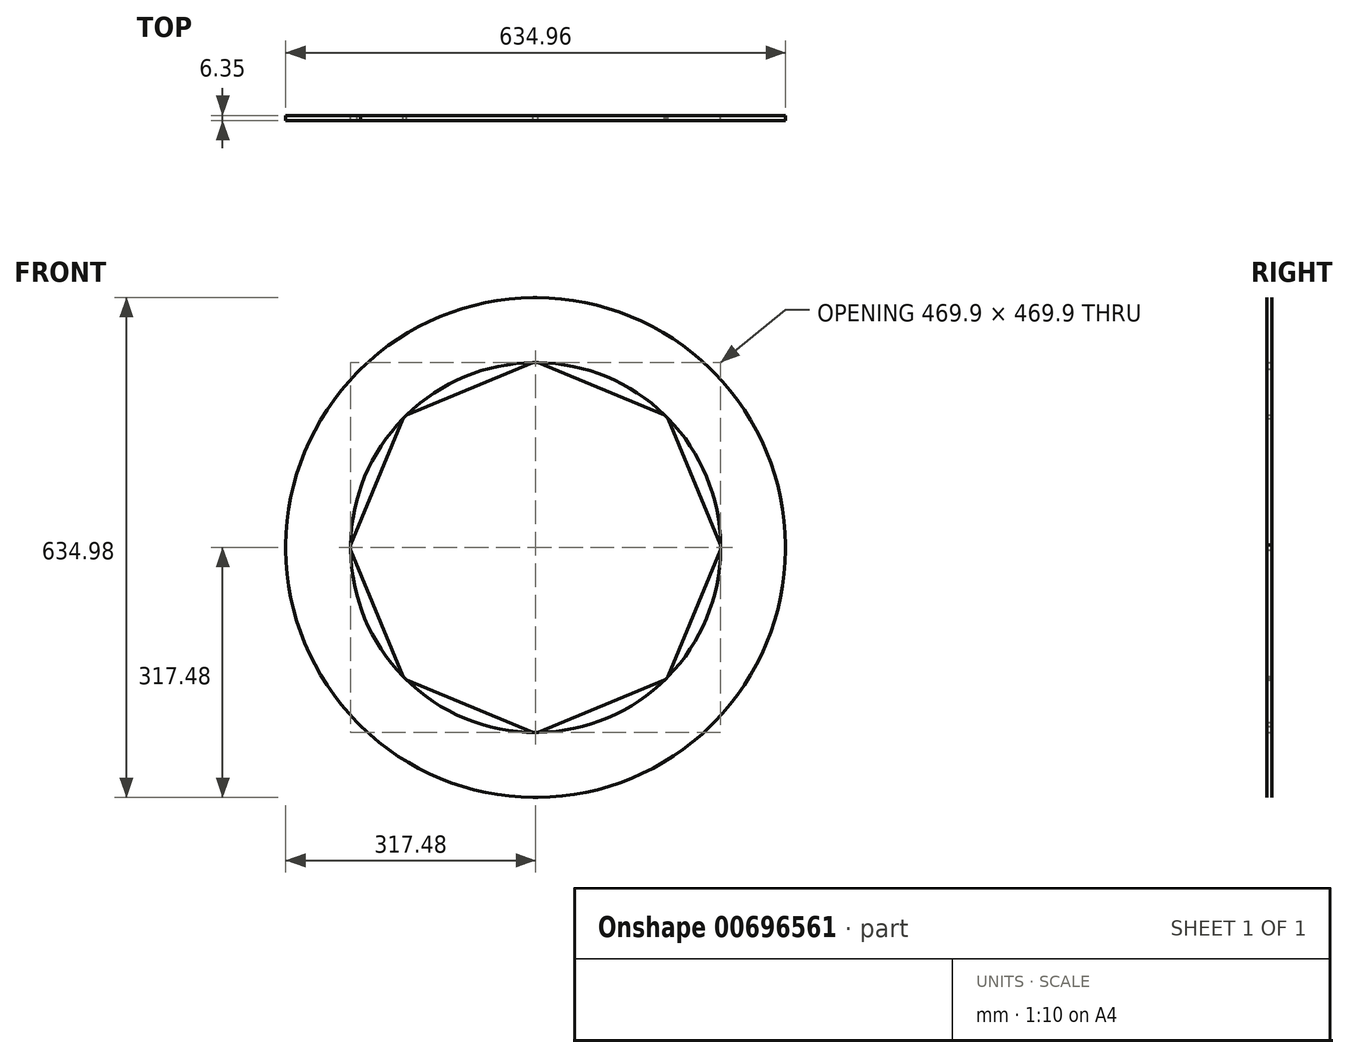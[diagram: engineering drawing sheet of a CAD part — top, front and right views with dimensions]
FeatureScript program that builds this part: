
annotation { "Feature Type Name" : "Feature", "Feature Type Description" : "" }
export const myFeature = defineFeature(function(context is Context, id is Id, definition is map)
    precondition{}
    {
        {
            var Q0;
            Q0=qCreatedBy(makeId("Front.planeOp"),FACE);
            var sketch = newSketch(context, id + "F0", { "sketchPlane" : qUnion([Q0])});
            skCircle(sketch, "E0", {"center": v(0, 0) * mm, "radius": 234.95 * mm});
            skCircle(sketch, "E1", {"center": v(0, 0) * mm, "radius": 317.5 * mm});
            skLineSegment(sketch, "E2", {"start": v(317.48, 0) * mm, "end": v(317.5, 0) * mm});
            skLineSegment(sketch, "E3", {"start": v(317.5, 0) * mm, "end": v(317.48, 0) * mm});
            skLineSegment(sketch, "E4", {"start": v(-317.48, 0) * mm, "end": v(-317.5, 0) * mm});
            skLineSegment(sketch, "E5", {"start": v(0, 317.5) * mm, "end": v(0, 317.5) * mm});
            skLineSegment(sketch, "E6", {"start": v(0, -317.48) * mm, "end": v(0, -317.5) * mm});
            skLineSegment(sketch, "E7.bottom", {"start": v(-317.5, 0) * mm, "end": v(-317.48, 0) * mm});
            skLineSegment(sketch, "E8", {"start": v(-224.5, 224.5) * mm, "end": v(-224.5, 224.5) * mm});
            skLineSegment(sketch, "E9", {"start": v(224.5, 224.5) * mm, "end": v(224.5, 224.5) * mm});
            skLineSegment(sketch, "E10", {"start": v(-224.5, -224.5) * mm, "end": v(-224.5, -224.5) * mm});
            skLineSegment(sketch, "E11", {"start": v(224.5, -224.5) * mm, "end": v(224.5, -224.5) * mm});
            skLineSegment(sketch, "E12", {"start": v(-166.13, -166.13) * mm, "end": v(-163.87, -168.36) * mm});
            skLineSegment(sketch, "E13", {"start": v(-166.13, -166.13) * mm, "end": v(-168.38, -163.89) * mm});
            skLineSegment(sketch, "E14", {"start": v(-168.38, -163.89) * mm, "end": v(-226.74, -222.25) * mm});
            skLineSegment(sketch, "E15", {"start": v(-163.87, -168.36) * mm, "end": v(-221.85, -227.13) * mm});
            skLineSegment(sketch, "E16", {"start": v(-221.85, -227.13) * mm, "end": v(-226.74, -222.25) * mm});
            skLineSegment(sketch, "E17", {"start": v(0, -234.95) * mm, "end": v(-3.17, -234.93) * mm});
            skLineSegment(sketch, "E18", {"start": v(0, -234.95) * mm, "end": v(3.18, -234.95) * mm});
            skLineSegment(sketch, "E19", {"start": v(-3.17, -234.93) * mm, "end": v(-3.17, -317.48) * mm});
            skLineSegment(sketch, "E20", {"start": v(3.18, -234.95) * mm, "end": v(3.18, -317.48) * mm});
            skLineSegment(sketch, "E21", {"start": v(3.18, -317.48) * mm, "end": v(-3.17, -317.48) * mm});
            skLineSegment(sketch, "E22", {"start": v(166.13, -166.13) * mm, "end": v(163.74, -168.22) * mm});
            skLineSegment(sketch, "E23", {"start": v(166.13, -166.13) * mm, "end": v(168.38, -163.89) * mm});
            skLineSegment(sketch, "E24", {"start": v(163.74, -168.22) * mm, "end": v(222.26, -226.73) * mm});
            skLineSegment(sketch, "E25", {"start": v(168.38, -163.89) * mm, "end": v(226.74, -222.25) * mm});
            skLineSegment(sketch, "E26", {"start": v(226.74, -222.25) * mm, "end": v(222.26, -226.73) * mm});
            skLineSegment(sketch, "E27", {"start": v(234.95, 0) * mm, "end": v(234.95, -3.17) * mm});
            skLineSegment(sketch, "E28", {"start": v(234.95, 0) * mm, "end": v(234.95, 3.18) * mm});
            skLineSegment(sketch, "E29", {"start": v(234.95, 3.18) * mm, "end": v(317.48, 3.18) * mm});
            skLineSegment(sketch, "E30", {"start": v(317.48, 3.18) * mm, "end": v(317.48, -3.18) * mm});
            skLineSegment(sketch, "E31", {"start": v(317.48, -3.18) * mm, "end": v(234.95, -3.17) * mm});
            skLineSegment(sketch, "E32", {"start": v(166.13, 166.13) * mm, "end": v(168.38, 163.89) * mm});
            skLineSegment(sketch, "E33", {"start": v(166.13, 166.13) * mm, "end": v(163.89, 168.38) * mm});
            skLineSegment(sketch, "E34", {"start": v(168.38, 163.89) * mm, "end": v(226.74, 222.25) * mm});
            skLineSegment(sketch, "E35", {"start": v(226.74, 222.25) * mm, "end": v(222.25, 226.74) * mm});
            skLineSegment(sketch, "E36", {"start": v(222.25, 226.74) * mm, "end": v(163.89, 168.38) * mm});
            skLineSegment(sketch, "E37", {"start": v(0, 234.95) * mm, "end": v(3.17, 234.95) * mm});
            skLineSegment(sketch, "E38", {"start": v(0, 234.95) * mm, "end": v(-3.17, 234.95) * mm});
            skLineSegment(sketch, "E39", {"start": v(-3.17, 234.95) * mm, "end": v(-3.17, 317.48) * mm});
            skLineSegment(sketch, "E40", {"start": v(-3.17, 317.48) * mm, "end": v(3.17, 317.5) * mm});
            skLineSegment(sketch, "E41", {"start": v(3.17, 317.5) * mm, "end": v(3.17, 234.95) * mm});
            skLineSegment(sketch, "E42", {"start": v(-166.13, 166.13) * mm, "end": v(-168.38, 163.89) * mm});
            skLineSegment(sketch, "E43", {"start": v(-166.13, 166.13) * mm, "end": v(-163.89, 168.38) * mm});
            skLineSegment(sketch, "E44", {"start": v(-168.38, 163.89) * mm, "end": v(-226.74, 222.25) * mm});
            skLineSegment(sketch, "E45", {"start": v(-226.74, 222.25) * mm, "end": v(-222.25, 226.74) * mm});
            skLineSegment(sketch, "E46", {"start": v(-222.25, 226.74) * mm, "end": v(-163.89, 168.38) * mm});
            skLineSegment(sketch, "E47", {"start": v(-234.95, 0) * mm, "end": v(-234.95, -3.18) * mm});
            skLineSegment(sketch, "E48", {"start": v(-234.95, 0) * mm, "end": v(-234.95, 3.17) * mm});
            skLineSegment(sketch, "E49", {"start": v(-234.95, 3.17) * mm, "end": v(-317.48, 3.17) * mm});
            skLineSegment(sketch, "E50", {"start": v(-317.48, 3.17) * mm, "end": v(-317.48, -3.18) * mm});
            skLineSegment(sketch, "E51", {"start": v(-317.48, -3.17) * mm, "end": v(-234.95, -3.18) * mm});
            skLineSegment(sketch, "E52", {"start": v(-163.89, 168.38) * mm, "end": v(-3.18, 234.95) * mm});
            skLineSegment(sketch, "E53", {"start": v(3.17, 234.95) * mm, "end": v(163.89, 168.38) * mm});
            skLineSegment(sketch, "E54", {"start": v(168.38, 163.89) * mm, "end": v(234.95, 3.18) * mm});
            skLineSegment(sketch, "E55", {"start": v(234.95, -3.18) * mm, "end": v(168.38, -163.89) * mm});
            skLineSegment(sketch, "E56", {"start": v(3.18, -234.95) * mm, "end": v(163.74, -168.22) * mm});
            skLineSegment(sketch, "E57", {"start": v(-3.17, -234.93) * mm, "end": v(-163.87, -168.36) * mm});
            skLineSegment(sketch, "E58", {"start": v(-168.38, -163.89) * mm, "end": v(-234.95, -3.18) * mm});
            skLineSegment(sketch, "E59", {"start": v(-234.95, 3.17) * mm, "end": v(-168.38, 163.89) * mm});
            skLineSegment(sketch, "E60", {"start": v(201.66, -83.53) * mm, "end": v(293.33, -121.5) * mm});
            skLineSegment(sketch, "E61", {"start": v(83.46, -201.58) * mm, "end": v(121.58, -293.3) * mm});
            skLineSegment(sketch, "E62", {"start": v(-201.66, -83.53) * mm, "end": v(-293.33, -121.5) * mm});
            skLineSegment(sketch, "E63", {"start": v(-201.66, 83.53) * mm, "end": v(-293.33, 121.5) * mm});
            skLineSegment(sketch, "E64", {"start": v(-83.53, 201.66) * mm, "end": v(-121.5, 293.33) * mm});
            skLineSegment(sketch, "E65", {"start": v(83.53, 201.66) * mm, "end": v(121.5, 293.33) * mm});
            skLineSegment(sketch, "E66", {"start": v(201.66, 83.53) * mm, "end": v(293.33, 121.5) * mm});
            skLineSegment(sketch, "E67.bottom", {"start": v(121.5, 293.33) * mm, "end": v(89.91, 293.33) * mm});
            skLineSegment(sketch, "E67.top", {"start": v(121.5, 217.07) * mm, "end": v(89.91, 217.07) * mm});
            skLineSegment(sketch, "E67.left", {"start": v(121.5, 293.33) * mm, "end": v(121.5, 217.07) * mm});
            skLineSegment(sketch, "E67.right", {"start": v(89.91, 293.33) * mm, "end": v(89.91, 217.07) * mm});
            skLineSegment(sketch, "E68.bottom", {"start": v(293.33, 121.5) * mm, "end": v(217.07, 121.5) * mm});
            skLineSegment(sketch, "E68.top", {"start": v(293.33, 89.91) * mm, "end": v(217.07, 89.91) * mm});
            skLineSegment(sketch, "E68.left", {"start": v(293.33, 121.5) * mm, "end": v(293.33, 89.91) * mm});
            skLineSegment(sketch, "E68.right", {"start": v(217.07, 121.5) * mm, "end": v(217.07, 89.91) * mm});
            skLineSegment(sketch, "E69.bottom", {"start": v(293.33, -121.5) * mm, "end": v(217.07, -121.5) * mm});
            skLineSegment(sketch, "E69.top", {"start": v(293.33, -89.91) * mm, "end": v(217.07, -89.91) * mm});
            skLineSegment(sketch, "E69.left", {"start": v(293.33, -121.5) * mm, "end": v(293.33, -89.91) * mm});
            skLineSegment(sketch, "E69.right", {"start": v(217.07, -121.5) * mm, "end": v(217.07, -89.91) * mm});
            skLineSegment(sketch, "E70.bottom", {"start": v(121.58, -293.3) * mm, "end": v(89.9, -293.3) * mm});
            skLineSegment(sketch, "E70.top", {"start": v(121.58, -217.07) * mm, "end": v(89.9, -217.07) * mm});
            skLineSegment(sketch, "E70.left", {"start": v(121.58, -293.3) * mm, "end": v(121.58, -217.07) * mm});
            skLineSegment(sketch, "E70.right", {"start": v(89.9, -293.3) * mm, "end": v(89.9, -217.07) * mm});
            skLineSegment(sketch, "E71.bottom", {"start": v(-293.33, -121.5) * mm, "end": v(-217.07, -121.5) * mm});
            skLineSegment(sketch, "E71.top", {"start": v(-293.33, -89.91) * mm, "end": v(-217.07, -89.91) * mm});
            skLineSegment(sketch, "E71.left", {"start": v(-293.33, -121.5) * mm, "end": v(-293.33, -89.91) * mm});
            skLineSegment(sketch, "E71.right", {"start": v(-217.07, -121.5) * mm, "end": v(-217.07, -89.91) * mm});
            skLineSegment(sketch, "E72.bottom", {"start": v(-293.33, 121.5) * mm, "end": v(-217.07, 121.5) * mm});
            skLineSegment(sketch, "E72.top", {"start": v(-293.33, 89.91) * mm, "end": v(-217.07, 89.91) * mm});
            skLineSegment(sketch, "E72.left", {"start": v(-293.33, 121.5) * mm, "end": v(-293.33, 89.91) * mm});
            skLineSegment(sketch, "E72.right", {"start": v(-217.07, 121.5) * mm, "end": v(-217.07, 89.91) * mm});
            skLineSegment(sketch, "E73.bottom", {"start": v(-121.5, 293.33) * mm, "end": v(-89.91, 293.33) * mm});
            skLineSegment(sketch, "E73.top", {"start": v(-121.5, 217.07) * mm, "end": v(-89.91, 217.07) * mm});
            skLineSegment(sketch, "E73.left", {"start": v(-121.5, 293.33) * mm, "end": v(-121.5, 217.07) * mm});
            skLineSegment(sketch, "E73.right", {"start": v(-89.91, 293.33) * mm, "end": v(-89.91, 217.07) * mm});
            skLineSegment(sketch, "E74", {"start": v(-83.52, -201.65) * mm, "end": v(-121.5, -293.33) * mm});
            skLineSegment(sketch, "E75.bottom", {"start": v(-121.5, -293.33) * mm, "end": v(-89.91, -293.33) * mm});
            skLineSegment(sketch, "E75.top", {"start": v(-121.5, -217.07) * mm, "end": v(-89.91, -217.07) * mm});
            skLineSegment(sketch, "E75.left", {"start": v(-121.5, -293.33) * mm, "end": v(-121.5, -217.07) * mm});
            skLineSegment(sketch, "E75.right", {"start": v(-89.91, -293.33) * mm, "end": v(-89.91, -217.07) * mm});
            skSolve(sketch);
        }
        {
            var Q0;
            {var subQ1=sQuery(id+"F0.wireOp",EDGE,"E51");Q0=makeQuery(id+"F0.imprint","IMPRINT",FACE,{"disambiguationData":[TD([[makeQuery(id+"F0.imprint","IMPRINT",EDGE,{"derivedFrom":subQ1}),-1.0]])]});}
            var Q1;
            {var subQ2=sQuery(id+"F0.wireOp",EDGE,"E71.top");Q1=makeQuery(id+"F0.imprint","IMPRINT",FACE,{"disambiguationData":[TD([[makeQuery(id+"F0.imprint","IMPRINT",EDGE,{"derivedFrom":subQ2}),-1.0]])]});}
            var Q2;
            {var subQ0=sQuery(id+"F0.wireOp",EDGE,"E71.bottom");Q2=makeQuery(id+"F0.imprint","IMPRINT",FACE,{"disambiguationData":[TD([[makeQuery(id+"F0.imprint","IMPRINT",EDGE,{"derivedFrom":subQ0}),1.0]])]});}
            var Q3;
            {var subQ1=sQuery(id+"F0.wireOp",EDGE,"E14");Q3=makeQuery(id+"F0.imprint","IMPRINT",FACE,{"disambiguationData":[TD([[makeQuery(id+"F0.imprint","IMPRINT",EDGE,{"derivedFrom":subQ1}),-1.0]])]});}
            var Q4;
            {var subQ1=sQuery(id+"F0.wireOp",EDGE,"E13");Q4=makeQuery(id+"F0.imprint","IMPRINT",FACE,{"disambiguationData":[TD([[makeQuery(id+"F0.imprint","IMPRINT",EDGE,{"derivedFrom":subQ1}),1.0]])]});}
            var Q5;
            {var subQ1=sQuery(id+"F0.wireOp",EDGE,"E15");Q5=makeQuery(id+"F0.imprint","IMPRINT",FACE,{"disambiguationData":[TD([[makeQuery(id+"F0.imprint","IMPRINT",EDGE,{"derivedFrom":subQ1}),1.0]])]});}
            var Q6;
            {var subQ2=sQuery(id+"F0.wireOp",EDGE,"E75.top");Q6=makeQuery(id+"F0.imprint","IMPRINT",FACE,{"disambiguationData":[TD([[makeQuery(id+"F0.imprint","IMPRINT",EDGE,{"derivedFrom":subQ2}),-1.0]])]});}
            var Q7;
            {var subQ0=sQuery(id+"F0.wireOp",EDGE,"E75.bottom");Q7=makeQuery(id+"F0.imprint","IMPRINT",FACE,{"disambiguationData":[TD([[makeQuery(id+"F0.imprint","IMPRINT",EDGE,{"derivedFrom":subQ0}),1.0]])]});}
            var Q8;
            {var subQ0=sQuery(id+"F0.wireOp",EDGE,"E19");Q8=makeQuery(id+"F0.imprint","IMPRINT",FACE,{"disambiguationData":[TD([[makeQuery(id+"F0.imprint","IMPRINT",EDGE,{"derivedFrom":subQ0}),-1.0]])]});}
            var Q9;
            {var subQ2=sQuery(id+"F0.wireOp",EDGE,"E18");Q9=makeQuery(id+"F0.imprint","IMPRINT",FACE,{"disambiguationData":[TD([[makeQuery(id+"F0.imprint","IMPRINT",EDGE,{"derivedFrom":subQ2}),-1.0]])]});}
            var Q10;
            {var subQ0=sQuery(id+"F0.wireOp",EDGE,"E20");Q10=makeQuery(id+"F0.imprint","IMPRINT",FACE,{"disambiguationData":[TD([[makeQuery(id+"F0.imprint","IMPRINT",EDGE,{"derivedFrom":subQ0}),1.0]])]});}
            var Q11;
            {var subQ0=sQuery(id+"F0.wireOp",EDGE,"E70.bottom");Q11=makeQuery(id+"F0.imprint","IMPRINT",FACE,{"disambiguationData":[TD([[makeQuery(id+"F0.imprint","IMPRINT",EDGE,{"derivedFrom":subQ0}),-1.0]])]});}
            var Q12;
            {var subQ2=sQuery(id+"F0.wireOp",EDGE,"E70.top");Q12=makeQuery(id+"F0.imprint","IMPRINT",FACE,{"disambiguationData":[TD([[makeQuery(id+"F0.imprint","IMPRINT",EDGE,{"derivedFrom":subQ2}),1.0]])]});}
            var Q13;
            {var subQ0=sQuery(id+"F0.wireOp",EDGE,"E70.top");Q13=makeQuery(id+"F0.imprint","IMPRINT",FACE,{"disambiguationData":[TD([[makeQuery(id+"F0.imprint","IMPRINT",EDGE,{"derivedFrom":subQ0}),-1.0]])]});}
            var Q14;
            {var subQ7=sQuery(id+"F0.wireOp",EDGE,"E23");Q14=makeQuery(id+"F0.imprint","IMPRINT",FACE,{"disambiguationData":[TD([[makeQuery(id+"F0.imprint","IMPRINT",EDGE,{"derivedFrom":subQ7}),-1.0]])]});}
            var Q15;
            {var subQ0=sQuery(id+"F0.wireOp",EDGE,"E25");Q15=makeQuery(id+"F0.imprint","IMPRINT",FACE,{"disambiguationData":[TD([[makeQuery(id+"F0.imprint","IMPRINT",EDGE,{"derivedFrom":subQ0}),1.0]])]});}
            var Q16;
            {var subQ0=sQuery(id+"F0.wireOp",EDGE,"E69.bottom");Q16=makeQuery(id+"F0.imprint","IMPRINT",FACE,{"disambiguationData":[TD([[makeQuery(id+"F0.imprint","IMPRINT",EDGE,{"derivedFrom":subQ0}),-1.0]])]});}
            var Q17;
            {var subQ2=sQuery(id+"F0.wireOp",EDGE,"E69.top");Q17=makeQuery(id+"F0.imprint","IMPRINT",FACE,{"disambiguationData":[TD([[makeQuery(id+"F0.imprint","IMPRINT",EDGE,{"derivedFrom":subQ2}),1.0]])]});}
            var Q18;
            {var subQ1=sQuery(id+"F0.wireOp",EDGE,"E31");Q18=makeQuery(id+"F0.imprint","IMPRINT",FACE,{"disambiguationData":[TD([[makeQuery(id+"F0.imprint","IMPRINT",EDGE,{"derivedFrom":subQ1}),1.0]])]});}
            var Q19;
            {var subQ1=sQuery(id+"F0.wireOp",EDGE,"E29");Q19=makeQuery(id+"F0.imprint","IMPRINT",FACE,{"disambiguationData":[TD([[makeQuery(id+"F0.imprint","IMPRINT",EDGE,{"derivedFrom":subQ1}),1.0]])]});}
            var Q20;
            {var subQ2=sQuery(id+"F0.wireOp",EDGE,"E68.top");Q20=makeQuery(id+"F0.imprint","IMPRINT",FACE,{"disambiguationData":[TD([[makeQuery(id+"F0.imprint","IMPRINT",EDGE,{"derivedFrom":subQ2}),-1.0]])]});}
            var Q21;
            {var subQ0=sQuery(id+"F0.wireOp",EDGE,"E68.bottom");Q21=makeQuery(id+"F0.imprint","IMPRINT",FACE,{"disambiguationData":[TD([[makeQuery(id+"F0.imprint","IMPRINT",EDGE,{"derivedFrom":subQ0}),1.0]])]});}
            var Q22;
            {var subQ0=sQuery(id+"F0.wireOp",EDGE,"E34");Q22=makeQuery(id+"F0.imprint","IMPRINT",FACE,{"disambiguationData":[TD([[makeQuery(id+"F0.imprint","IMPRINT",EDGE,{"derivedFrom":subQ0}),-1.0]])]});}
            var Q23;
            {var subQ1=sQuery(id+"F0.wireOp",EDGE,"E36");Q23=makeQuery(id+"F0.imprint","IMPRINT",FACE,{"disambiguationData":[TD([[makeQuery(id+"F0.imprint","IMPRINT",EDGE,{"derivedFrom":subQ1}),-1.0]])]});}
            var Q24;
            Q24=makeQuery(id+"F0.imprint","IMPRINT",FACE,{"disambiguationData":[TD([[makeQuery(id+"F0.imprint","IMPRINT",EDGE,{"derivedFrom":sQuery(id+"F0.wireOp",EDGE,"E27")}),1.0]])]});
            var Q25;
            Q25=makeQuery(id+"F0.imprint","IMPRINT",FACE,{"disambiguationData":[TD([[makeQuery(id+"F0.imprint","IMPRINT",EDGE,{"derivedFrom":sQuery(id+"F0.wireOp",EDGE,"E32")}),1.0]])]});
            var Q26;
            {var subQ2=sQuery(id+"F0.wireOp",EDGE,"E67.top");Q26=makeQuery(id+"F0.imprint","IMPRINT",FACE,{"disambiguationData":[TD([[makeQuery(id+"F0.imprint","IMPRINT",EDGE,{"derivedFrom":subQ2}),-1.0]])]});}
            var Q27;
            {var subQ0=sQuery(id+"F0.wireOp",EDGE,"E67.bottom");Q27=makeQuery(id+"F0.imprint","IMPRINT",FACE,{"disambiguationData":[TD([[makeQuery(id+"F0.imprint","IMPRINT",EDGE,{"derivedFrom":subQ0}),1.0]])]});}
            var Q28;
            {var subQ5=sQuery(id+"F0.wireOp",EDGE,"E67.bottom");Q28=makeQuery(id+"F0.imprint","IMPRINT",FACE,{"disambiguationData":[TD([[makeQuery(id+"F0.imprint","IMPRINT",EDGE,{"derivedFrom":subQ5}),-1.0]])]});}
            var Q29;
            {var subQ0=sQuery(id+"F0.wireOp",EDGE,"E39");Q29=makeQuery(id+"F0.imprint","IMPRINT",FACE,{"disambiguationData":[TD([[makeQuery(id+"F0.imprint","IMPRINT",EDGE,{"derivedFrom":subQ0}),1.0]])]});}
            var Q30;
            {var subQ6=sQuery(id+"F0.wireOp",EDGE,"E37");Q30=makeQuery(id+"F0.imprint","IMPRINT",FACE,{"disambiguationData":[TD([[makeQuery(id+"F0.imprint","IMPRINT",EDGE,{"derivedFrom":subQ6}),1.0]])]});}
            var Q31;
            {var subQ0=sQuery(id+"F0.wireOp",EDGE,"E73.bottom");Q31=makeQuery(id+"F0.imprint","IMPRINT",FACE,{"disambiguationData":[TD([[makeQuery(id+"F0.imprint","IMPRINT",EDGE,{"derivedFrom":subQ0}),-1.0]])]});}
            var Q32;
            {var subQ2=sQuery(id+"F0.wireOp",EDGE,"E73.top");Q32=makeQuery(id+"F0.imprint","IMPRINT",FACE,{"disambiguationData":[TD([[makeQuery(id+"F0.imprint","IMPRINT",EDGE,{"derivedFrom":subQ2}),1.0]])]});}
            var Q33;
            {var subQ1=sQuery(id+"F0.wireOp",EDGE,"E46");Q33=makeQuery(id+"F0.imprint","IMPRINT",FACE,{"disambiguationData":[TD([[makeQuery(id+"F0.imprint","IMPRINT",EDGE,{"derivedFrom":subQ1}),1.0]])]});}
            var Q34;
            Q34=makeQuery(id+"F0.imprint","IMPRINT",FACE,{"disambiguationData":[TD([[makeQuery(id+"F0.imprint","IMPRINT",EDGE,{"derivedFrom":sQuery(id+"F0.wireOp",EDGE,"E42")}),-1.0]])]});
            var Q35;
            {var subQ1=sQuery(id+"F0.wireOp",EDGE,"E44");Q35=makeQuery(id+"F0.imprint","IMPRINT",FACE,{"disambiguationData":[TD([[makeQuery(id+"F0.imprint","IMPRINT",EDGE,{"derivedFrom":subQ1}),1.0]])]});}
            var Q36;
            {var subQ0=sQuery(id+"F0.wireOp",EDGE,"E72.bottom");Q36=makeQuery(id+"F0.imprint","IMPRINT",FACE,{"disambiguationData":[TD([[makeQuery(id+"F0.imprint","IMPRINT",EDGE,{"derivedFrom":subQ0}),-1.0]])]});}
            var Q37;
            {var subQ2=sQuery(id+"F0.wireOp",EDGE,"E72.top");Q37=makeQuery(id+"F0.imprint","IMPRINT",FACE,{"disambiguationData":[TD([[makeQuery(id+"F0.imprint","IMPRINT",EDGE,{"derivedFrom":subQ2}),1.0]])]});}
            var Q38;
            Q38=makeQuery(id+"F0.imprint","IMPRINT",FACE,{"disambiguationData":[TD([[makeQuery(id+"F0.imprint","IMPRINT",EDGE,{"derivedFrom":sQuery(id+"F0.wireOp",EDGE,"E47")}),-1.0]])]});
            var Q39;
            {var subQ0=sQuery(id+"F0.wireOp",EDGE,"E49");Q39=makeQuery(id+"F0.imprint","IMPRINT",FACE,{"disambiguationData":[TD([[makeQuery(id+"F0.imprint","IMPRINT",EDGE,{"derivedFrom":subQ0}),-1.0]])]});}
            var Q40;
            {var subQ20=sQuery(id+"F0.wireOp",EDGE,"E12");Q40=makeQuery(id+"F0.imprint","IMPRINT",FACE,{"disambiguationData":[TD([[makeQuery(id+"F0.imprint","IMPRINT",EDGE,{"derivedFrom":subQ20}),1.0]])]});}
            extrude(context, id + "F1", {"entities" : qUnion([Q0, Q1, Q2, Q3, Q4, Q5, Q6, Q7, Q8, Q9, Q10, Q11, Q12, Q13, Q14, Q15, Q16, Q17, Q18, Q19, Q20, Q21, Q22, Q23, Q24, Q25, Q26, Q27, Q28, Q29, Q30, Q31, Q32, Q33, Q34, Q35, Q36, Q37, Q38, Q39, Q40]), "depth" : 6.35 * mm, "offsetDistance" : 25.4 * mm});
        }
    });
